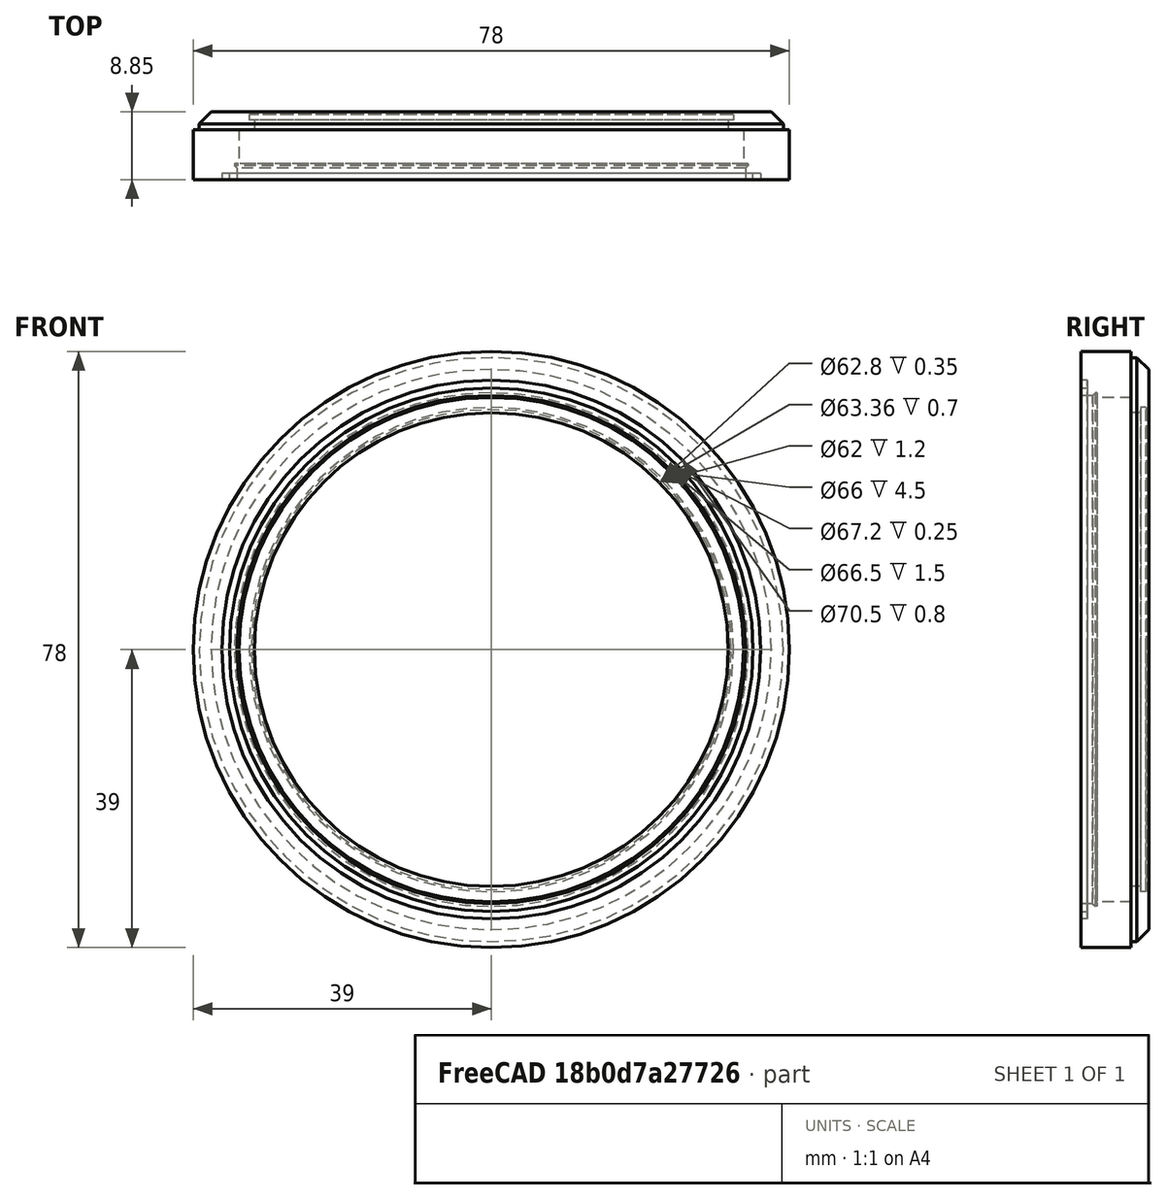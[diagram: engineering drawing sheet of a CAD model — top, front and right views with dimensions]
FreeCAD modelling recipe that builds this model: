
FCSTD DOCUMENT  (FreeCAD 0.15R4671 (Git))
Label: Case2-dimensioned
License: All rights reserved
LicenseURL: http://en.wikipedia.org/wiki/All_rights_reserved
objects: Sketcher::SketchObject×1, PartDesign::Revolution×1
note: 3 computed .brp shape members not serialized (recipe doc carries the construction recipe); baked Part::Feature solids carry a one-line shape summary decoded from their .brp

FEATURE [Sketcher::SketchObject] Sketch
  sketch-geometry (21):
    g0: LineSegment StartX=39 StartY=0 StartZ=0 EndX=39 EndY=6.5 EndZ=0
    g1: LineSegment StartX=39 StartY=6.5 StartZ=0 EndX=38.2 EndY=6.5 EndZ=0
    g2: LineSegment StartX=38.2 StartY=6.5 StartZ=0 EndX=38.2 EndY=7.3 EndZ=0
    g3: LineSegment StartX=38.2 StartY=7.3 StartZ=0 EndX=36.65 EndY=8.85 EndZ=0
    g4: LineSegment StartX=36.65 StartY=8.85 StartZ=0 EndX=31.4 EndY=8.85 EndZ=0
    g5: LineSegment StartX=31.4 StartY=8.85 StartZ=0 EndX=31.4 EndY=8.5 EndZ=0
    g6: LineSegment StartX=31.4 StartY=8.5 StartZ=0 EndX=31.68 EndY=8.5 EndZ=0
    g7: LineSegment StartX=31.68 StartY=8.5 StartZ=0 EndX=31.68 EndY=7.8 EndZ=0
    g8: LineSegment StartX=31.68 StartY=7.8 StartZ=0 EndX=31 EndY=7.8 EndZ=0
    g9: LineSegment StartX=31 StartY=7.8 StartZ=0 EndX=31 EndY=6.6 EndZ=0
    g10: LineSegment StartX=31 StartY=6.6 StartZ=0 EndX=33 EndY=6.6 EndZ=0
    g11: LineSegment StartX=33 StartY=6.6 StartZ=0 EndX=33 EndY=2.1 EndZ=0
    g12: LineSegment StartX=33 StartY=2.1 StartZ=0 EndX=33.6 EndY=2.1 EndZ=0
    g13: LineSegment StartX=33.6 StartY=2.1 StartZ=0 EndX=33.6 EndY=1.85 EndZ=0
    g14: LineSegment StartX=33.6 StartY=1.85 StartZ=0 EndX=33.25 EndY=1.5 EndZ=0
    g15: LineSegment StartX=33.25 StartY=1.5 StartZ=0 EndX=33.25 EndY=0 EndZ=0
    g16: LineSegment StartX=33.25 StartY=0 StartZ=0 EndX=34.25 EndY=0 EndZ=0
    g17: LineSegment StartX=34.25 StartY=0 StartZ=0 EndX=34.25 EndY=0.8 EndZ=0
    g18: LineSegment StartX=34.25 StartY=0.8 StartZ=0 EndX=35.25 EndY=0.8 EndZ=0
    g19: LineSegment StartX=35.25 StartY=0.8 StartZ=0 EndX=35.25 EndY=0 EndZ=0
    g20: LineSegment StartX=35.25 StartY=0 StartZ=0 EndX=39 EndY=0 EndZ=0
  constraints (63):
    c: Vertical(g0)
    c: Coincident(g0,g1)
    c: Horizontal(g1)
    c: Coincident(g1,g2)
    c: Coincident(g2,g3)
    c: Coincident(g3,g4)
    c: Horizontal(g4)
    c: Coincident(g4,g5)
    c: Coincident(g5,g6)
    c: Horizontal(g6)
    c: Coincident(g6,g7)
    c: Coincident(g7,g8)
    c: Coincident(g8,g9)
    c: Coincident(g9,g10)
    c: Coincident(g10,g11)
    c: Vertical(g11)
    c: Coincident(g11,g12)
    c: Coincident(g12,g13)
    c: Vertical(g13)
    c: Coincident(g13,g14)
    c: Vertical(g15)
    c: Coincident(g15,g16)
    c: Coincident(g16,g17)
    c: Coincident(g17,g18)
    c: Horizontal(g18)
    c: Coincident(g18,g19)
    c: Coincident(g19,g20)
    c: Coincident(g20,g0)
    c: Horizontal(g8)
    c: Horizontal(g10)
    c: Vertical(g9)
    c: Vertical(g5)
    c: Vertical(g7)
    c: Horizontal(g20)
    c: Vertical(g19)
    c: Horizontal(g16)
    c: Vertical(g17)
    c: Horizontal(g12)
    c: Vertical(g2)
    c: DistanceY(g0,g0) = -6.5
    c: DistanceX(g1,g0) = 0.8
    c: DistanceY(g2,g1) = -0.8
    c: DistanceY(g3,g0) = -2.35
    c: DistanceY(g4,g5) = -0.35
    c: DistanceY(g8,g9) = -1.2
    c: DistanceY(g10,g11) = -4.5
    c: DistanceY(g6,g7) = -0.7
    c: DistanceX(g17,g18) = 1
    c: Angle(g4,g3) = 2.35619
    c: DistanceX(g0) = 39
    c: DistanceX(g8) = 31
    c: DistanceY(g17,g16) = -0.8
    c: DistanceY(g19) = -0.8
    c: DistanceX(g9,g10) = 2
    c: DistanceX(g4) = 31.4
    c: DistanceX(g5,g6) = 0.28
    c: DistanceY(g0) = 0
    c: DistanceX(g14) = 33.25
    c: Coincident(g14,g15)
    c: DistanceY(g15,g14) = 1.5
    c: DistanceX(g11,g12) = 0.6
    c: Angle(g13,g14) = 2.35619
    c: DistanceX(g15,g16) = 1
FEATURE [PartDesign::Revolution] Revolution
  Angle = 360
  Axis = (0,1,0)
  Base = (0,0,0)
  ReferenceAxis = -> Sketch [V_Axis]
  Reversed = true
  Sketch = -> Sketch
